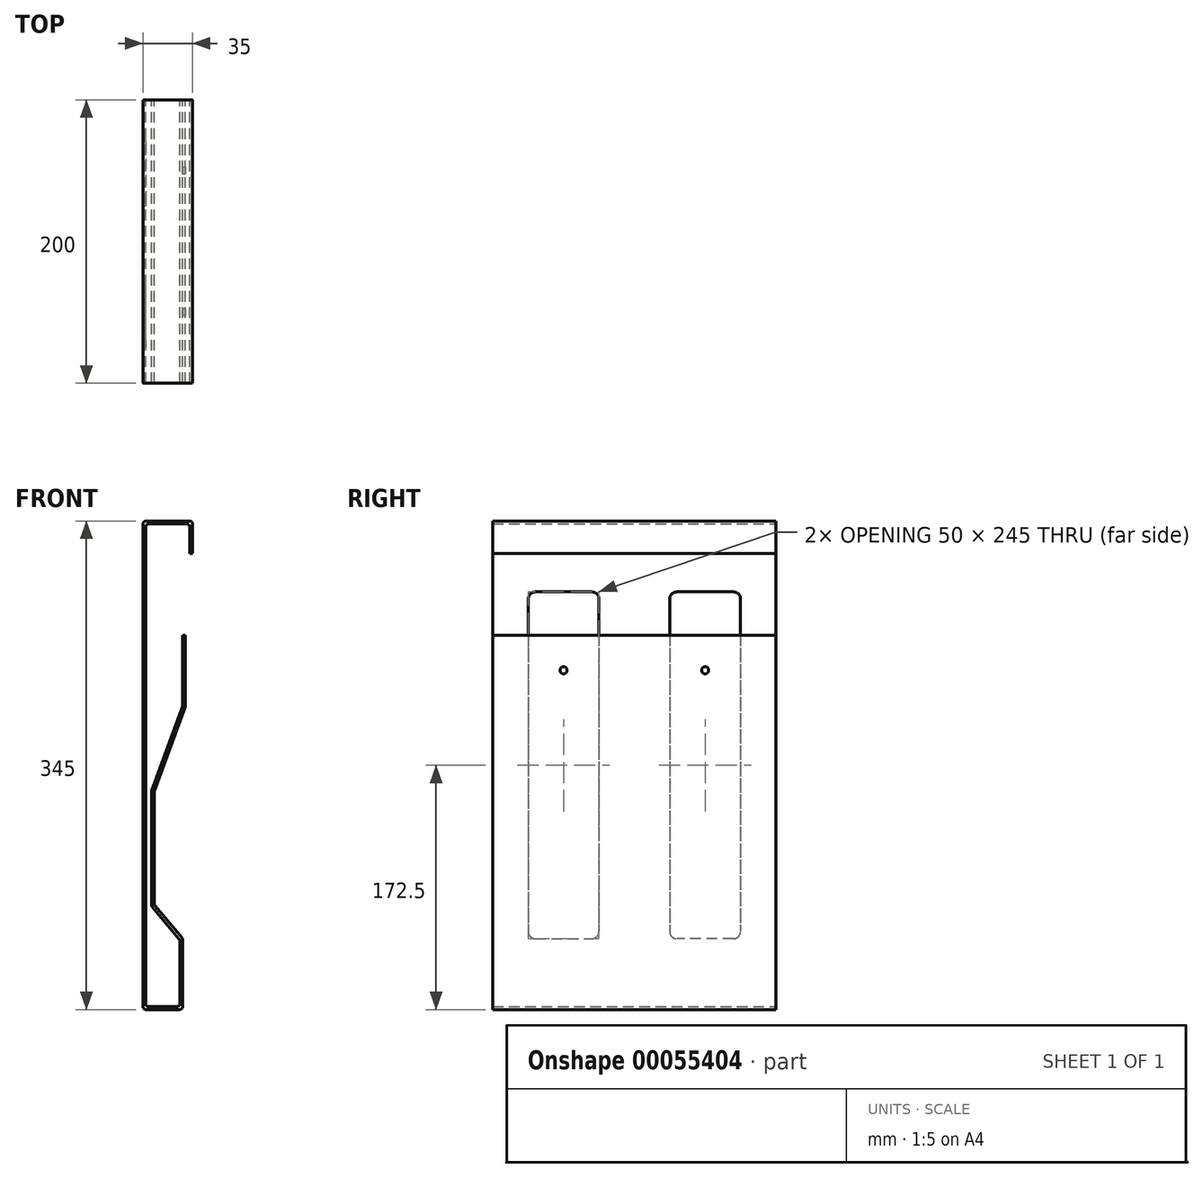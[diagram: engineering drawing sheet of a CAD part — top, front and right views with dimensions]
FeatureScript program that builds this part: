
annotation { "Feature Type Name" : "Feature", "Feature Type Description" : "" }
export const myFeature = defineFeature(function(context is Context, id is Id, definition is map)
    precondition{}
    {
        {
            var Q0;
            Q0=qCreatedBy(makeId("Front.planeOp"),FACE);
            var sketch = newSketch(context, id + "F0", { "sketchPlane" : qUnion([Q0])});
            skLineSegment(sketch, "E0", {"start": v(0, 0) * mm, "end": v(35, 0) * mm});
            skLineSegment(sketch, "E1", {"start": v(35, 0) * mm, "end": v(35, -23) * mm});
            skLineSegment(sketch, "E2", {"start": v(0, 0) * mm, "end": v(0, -345) * mm});
            skLineSegment(sketch, "E3", {"start": v(0, -345) * mm, "end": v(28, -345) * mm});
            skLineSegment(sketch, "E4", {"start": v(28, -295) * mm, "end": v(28, -345) * mm});
            skLineSegment(sketch, "E5.0", {"start": v(33, -2) * mm, "end": v(33, -23) * mm});
            skLineSegment(sketch, "E5.1", {"start": v(26, -295.73) * mm, "end": v(26, -343) * mm});
            skLineSegment(sketch, "E5.2", {"start": v(2, -343) * mm, "end": v(26, -343) * mm});
            skLineSegment(sketch, "E5.3", {"start": v(2, -2) * mm, "end": v(2, -343) * mm});
            skLineSegment(sketch, "E5.4", {"start": v(2, -2) * mm, "end": v(33, -2) * mm});
            skLineSegment(sketch, "E6", {"start": v(33, -23) * mm, "end": v(35, -23) * mm});
            skLineSegment(sketch, "E7", {"start": v(26, -295.73) * mm, "end": v(6, -271.9) * mm});
            skLineSegment(sketch, "E8", {"start": v(6, -271.9) * mm, "end": v(6, -190.81) * mm});
            skLineSegment(sketch, "E9", {"start": v(6, -190.81) * mm, "end": v(28, -130.37) * mm});
            skLineSegment(sketch, "E10", {"start": v(28, -130.37) * mm, "end": v(28, -80.72) * mm});
            skLineSegment(sketch, "E11.0", {"start": v(30, -130.72) * mm, "end": v(30, -80.72) * mm});
            skLineSegment(sketch, "E11.1", {"start": v(8, -191.16) * mm, "end": v(30, -130.72) * mm});
            skLineSegment(sketch, "E11.2", {"start": v(8, -271.16) * mm, "end": v(8, -191.16) * mm});
            skLineSegment(sketch, "E11.3", {"start": v(28, -295) * mm, "end": v(8, -271.16) * mm});
            skLineSegment(sketch, "E12", {"start": v(28, -80.72) * mm, "end": v(30, -80.72) * mm});
            skSolve(sketch);
        }
        {
            var Q0;
            Q0=qSketchRegion(id+"F0",true);
            extrude(context, id + "F1", {"entities" : qUnion([Q0]), "depth" : 200 * mm});
        }
        {
            var Q0;
            Q0=makeQuery(id+"F1.opExtrude","SWEPT_EDGE",EDGE,{"disambiguationData":[OSD([sQuery(id+"F0.wireOp",EDGE,"E0"),sQuery(id+"F0.wireOp",EDGE,"E2")])]});
            var Q1;
            Q1=makeQuery(id+"F1.opExtrude","SWEPT_EDGE",EDGE,{"disambiguationData":[OSD([sQuery(id+"F0.wireOp",EDGE,"E0"),sQuery(id+"F0.wireOp",EDGE,"E1")])]});
            var Q2;
            Q2=makeQuery(id+"F1.opExtrude","SWEPT_EDGE",EDGE,{"disambiguationData":[OSD([sQuery(id+"F0.wireOp",EDGE,"E5.0"),sQuery(id+"F0.wireOp",EDGE,"E5.4")])]});
            var Q3;
            Q3=makeQuery(id+"F1.opExtrude","SWEPT_EDGE",EDGE,{"disambiguationData":[OSD([sQuery(id+"F0.wireOp",EDGE,"E5.3"),sQuery(id+"F0.wireOp",EDGE,"E5.4")])]});
            var Q4;
            Q4=makeQuery(id+"F1.opExtrude","SWEPT_EDGE",EDGE,{"disambiguationData":[OSD([sQuery(id+"F0.wireOp",EDGE,"E2"),sQuery(id+"F0.wireOp",EDGE,"E3")])]});
            var Q5;
            Q5=makeQuery(id+"F1.opExtrude","SWEPT_EDGE",EDGE,{"disambiguationData":[OSD([sQuery(id+"F0.wireOp",EDGE,"E5.2"),sQuery(id+"F0.wireOp",EDGE,"E5.3")])]});
            var Q6;
            Q6=makeQuery(id+"F1.opExtrude","SWEPT_EDGE",EDGE,{"disambiguationData":[OSD([sQuery(id+"F0.wireOp",EDGE,"E3"),sQuery(id+"F0.wireOp",EDGE,"E4")])]});
            var Q7;
            Q7=makeQuery(id+"F1.opExtrude","SWEPT_EDGE",EDGE,{"disambiguationData":[OSD([sQuery(id+"F0.wireOp",EDGE,"E5.1"),sQuery(id+"F0.wireOp",EDGE,"E5.2")])]});
            var Q8;
            Q8=makeQuery(id+"F1.opExtrude","SWEPT_EDGE",EDGE,{"disambiguationData":[OSD([sQuery(id+"F0.wireOp",EDGE,"E5.1"),sQuery(id+"F0.wireOp",EDGE,"E7")])]});
            var Q9;
            Q9=makeQuery(id+"F1.opExtrude","SWEPT_EDGE",EDGE,{"disambiguationData":[OSD([sQuery(id+"F0.wireOp",EDGE,"E4"),sQuery(id+"F0.wireOp",EDGE,"E11.3")])]});
            var Q10;
            Q10=makeQuery(id+"F1.opExtrude","SWEPT_EDGE",EDGE,{"disambiguationData":[OSD([sQuery(id+"F0.wireOp",EDGE,"E11.2"),sQuery(id+"F0.wireOp",EDGE,"E11.3")])]});
            var Q11;
            Q11=makeQuery(id+"F1.opExtrude","SWEPT_EDGE",EDGE,{"disambiguationData":[OSD([sQuery(id+"F0.wireOp",EDGE,"E7"),sQuery(id+"F0.wireOp",EDGE,"E8")])]});
            var Q12;
            Q12=makeQuery(id+"F1.opExtrude","SWEPT_EDGE",EDGE,{"disambiguationData":[OSD([sQuery(id+"F0.wireOp",EDGE,"E8"),sQuery(id+"F0.wireOp",EDGE,"E9")])]});
            var Q13;
            Q13=makeQuery(id+"F1.opExtrude","SWEPT_EDGE",EDGE,{"disambiguationData":[OSD([sQuery(id+"F0.wireOp",EDGE,"E11.1"),sQuery(id+"F0.wireOp",EDGE,"E11.2")])]});
            var Q14;
            Q14=makeQuery(id+"F1.opExtrude","SWEPT_EDGE",EDGE,{"disambiguationData":[OSD([sQuery(id+"F0.wireOp",EDGE,"E11.0"),sQuery(id+"F0.wireOp",EDGE,"E11.1")])]});
            var Q15;
            Q15=makeQuery(id+"F1.opExtrude","SWEPT_EDGE",EDGE,{"disambiguationData":[OSD([sQuery(id+"F0.wireOp",EDGE,"E9"),sQuery(id+"F0.wireOp",EDGE,"E10")])]});
            fillet(context, id + "F2", {"entities" : qUnion([Q0, Q1, Q2, Q3, Q4, Q5, Q6, Q7, Q8, Q9, Q10, Q11, Q12, Q13, Q14, Q15]), "radius" : 2 * mm, "tangentPropagation" : true, "allowEdgeOverflow" : false});
        }
        {
            var Q0;
            Q0=makeQuery(id+"F1.opExtrude","SWEPT_FACE",FACE,{"disambiguationData":[OSD([sQuery(id+"F0.wireOp",EDGE,"E2")])]});
            var sketch = newSketch(context, id + "F3", { "sketchPlane" : qUnion([Q0])});
            skLineSegment(sketch, "E13", {"start": v(100, -2) * mm, "end": v(100, -38.74) * mm, "construction": true});
            skLineSegment(sketch, "E14.bottom", {"start": v(30, -50) * mm, "end": v(70, -50) * mm});
            skLineSegment(sketch, "E14.top", {"start": v(30, -295) * mm, "end": v(70, -295) * mm});
            skLineSegment(sketch, "E14.left", {"start": v(25, -55) * mm, "end": v(25, -290) * mm});
            skLineSegment(sketch, "E14.right", {"start": v(75, -55) * mm, "end": v(75, -290) * mm});
            skPoint(sketch, "E15.visualSharp", {"position": v(25, -50) * mm});
            skArc(sketch, "E15.filletArc", {"start": v(30, -50) * mm, "mid": v(26.46, -51.46) * mm, "end": v(25, -55) * mm});
            skPoint(sketch, "E16.visualSharp", {"position": v(75, -50) * mm});
            skArc(sketch, "E16.filletArc", {"start": v(75, -55) * mm, "mid": v(73.54, -51.46) * mm, "end": v(70, -50) * mm});
            skPoint(sketch, "E17.visualSharp", {"position": v(75, -295) * mm});
            skArc(sketch, "E17.filletArc", {"start": v(70, -295) * mm, "mid": v(73.54, -293.54) * mm, "end": v(75, -290) * mm});
            skPoint(sketch, "E18.visualSharp", {"position": v(25, -295) * mm});
            skArc(sketch, "E18.filletArc", {"start": v(25, -290) * mm, "mid": v(26.46, -293.54) * mm, "end": v(30, -295) * mm});
            skArc(sketch, "E19.MirrorCS", {"start": v(130, -295) * mm, "mid": v(126.46, -293.54) * mm, "end": v(125, -290) * mm});
            skArc(sketch, "E20.MirrorCS", {"start": v(125, -55) * mm, "mid": v(126.46, -51.46) * mm, "end": v(130, -50) * mm});
            skArc(sketch, "E21.MirrorCS", {"start": v(175, -290) * mm, "mid": v(173.54, -293.54) * mm, "end": v(170, -295) * mm});
            skArc(sketch, "E22.MirrorCS", {"start": v(170, -50) * mm, "mid": v(173.54, -51.46) * mm, "end": v(175, -55) * mm});
            skPoint(sketch, "E23.MirrorP", {"position": v(175, -295) * mm});
            skLineSegment(sketch, "E24.MirrorCS", {"start": v(170, -50) * mm, "end": v(130, -50) * mm});
            skPoint(sketch, "E25.MirrorP", {"position": v(125, -295) * mm});
            skLineSegment(sketch, "E26.MirrorCS", {"start": v(170, -295) * mm, "end": v(130, -295) * mm});
            skLineSegment(sketch, "E27.MirrorCS", {"start": v(175, -55) * mm, "end": v(175, -290) * mm});
            skPoint(sketch, "E28.MirrorP", {"position": v(175, -50) * mm});
            skPoint(sketch, "E29.MirrorP", {"position": v(125, -50) * mm});
            skLineSegment(sketch, "E30.MirrorCS", {"start": v(125, -55) * mm, "end": v(125, -290) * mm});
            skSolve(sketch);
        }
        {
            var Q0;
            Q0 = qSketchRegion(id + "F3", true);
            extrude(context, id + "F4", {"entities" : qUnion([Q0]), "operationType" : NewBodyOperationType.REMOVE, "oppositeDirection" : true, "depth" : 2 * mm});
        }
        {
            var Q0;
            Q0=makeQuery(id+"F1.opExtrude","SWEPT_FACE",FACE,{"disambiguationData":[OSD([sQuery(id+"F0.wireOp",EDGE,"E10")])]});
            var sketch = newSketch(context, id + "F5", { "sketchPlane" : qUnion([Q0])});
            skLineSegment(sketch, "E31", {"start": v(0, -105.37) * mm, "end": v(200, -105.37) * mm, "construction": true});
            skPoint(sketch, "E32", {"position": v(50, -105.37) * mm});
            skPoint(sketch, "E33", {"position": v(150, -105.37) * mm});
            skSolve(sketch);
        }
        {
            var Q0;
            Q0=sQuery(id+"F5.wireOp",VERTEX,"E32");
            var Q1;
            Q1=sQuery(id+"F5.wireOp",VERTEX,"E33");
            var Q2;
            Q2=makeQuery(id+"F1.opExtrude","SWEPT_BODY",BODY,{"disambiguationData":[OSD([sQuery(id+"F0.wireOp",EDGE,"E0"),sQuery(id+"F0.wireOp",EDGE,"E1"),sQuery(id+"F0.wireOp",EDGE,"E2"),sQuery(id+"F0.wireOp",EDGE,"E3"),sQuery(id+"F0.wireOp",EDGE,"E4"),sQuery(id+"F0.wireOp",EDGE,"E5.0"),sQuery(id+"F0.wireOp",EDGE,"E5.1"),sQuery(id+"F0.wireOp",EDGE,"E5.2"),sQuery(id+"F0.wireOp",EDGE,"E5.3"),sQuery(id+"F0.wireOp",EDGE,"E5.4"),sQuery(id+"F0.wireOp",EDGE,"E6"),sQuery(id+"F0.wireOp",EDGE,"E7"),sQuery(id+"F0.wireOp",EDGE,"E8"),sQuery(id+"F0.wireOp",EDGE,"E9"),sQuery(id+"F0.wireOp",EDGE,"E10"),sQuery(id+"F0.wireOp",EDGE,"E11.0"),sQuery(id+"F0.wireOp",EDGE,"E11.1"),sQuery(id+"F0.wireOp",EDGE,"E11.2"),sQuery(id+"F0.wireOp",EDGE,"E11.3"),sQuery(id+"F0.wireOp",EDGE,"E12")])]});
            hole(context, id + "F6", {"style" : HoleStyle.SIMPLE, "endStyle" : HoleEndStyle.BLIND, "holeDiameter" : 5 * mm, "holeDepth" : 2 * mm, "locations" : qUnion([Q0, Q1]), "scope" : qUnion([Q2])});
        }
    });
